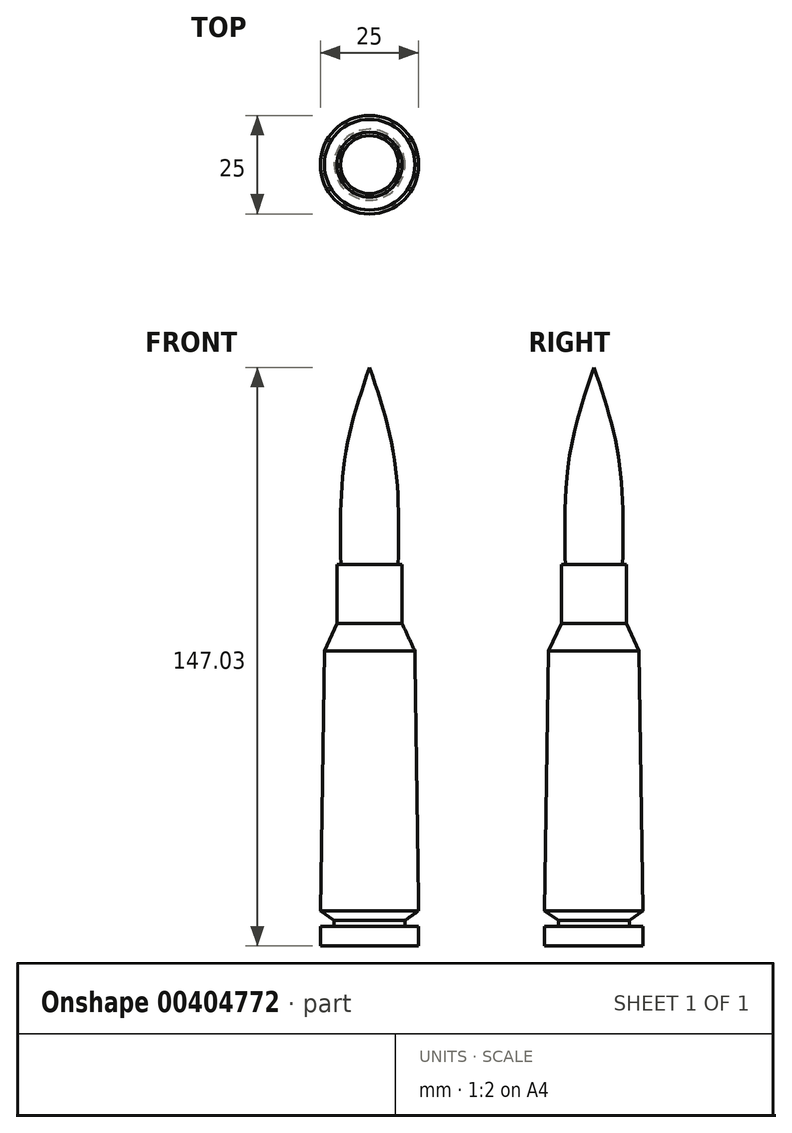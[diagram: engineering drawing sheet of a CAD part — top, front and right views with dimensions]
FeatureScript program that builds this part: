
annotation { "Feature Type Name" : "Feature", "Feature Type Description" : "" }
export const myFeature = defineFeature(function(context is Context, id is Id, definition is map)
    precondition{}
    {
        {
            var Q0;
            Q0=qCreatedBy(makeId("Top.planeOp"),FACE);
            var sketch = newSketch(context, id + "F0", { "sketchPlane" : qUnion([Q0])});
            skCircle(sketch, "E0", {"center": v(0, 0) * mm, "radius": 12.5 * mm});
            skSolve(sketch);
        }
        {
            var Q0;
            Q0=qSketchRegion(id+"F0",true);
            extrude(context, id + "F1", {"entities" : qUnion([Q0]), "depth" : 5 * mm});
        }
        {
            var Q0;
            Q0=makeQuery(id+"F1.opExtrude","CAP_FACE",FACE,{"disambiguationData":[OSD([sQuery(id+"F0.wireOp",EDGE,"E0")])],"isStart":false});
            var sketch = newSketch(context, id + "F2", { "sketchPlane" : qUnion([Q0])});
            skCircle(sketch, "E1", {"center": v(0, 0) * mm, "radius": 9 * mm});
            skSolve(sketch);
        }
        {
            var Q0;
            Q0=qSketchRegion(id+"F2",true);
            extrude(context, id + "F3", {"entities" : qUnion([Q0]), "operationType" : NewBodyOperationType.ADD, "depth" : 1.5 * mm});
        }
        {
            var Q0;
            Q0=qCreatedBy(makeId("Top.planeOp"),FACE);
            cPlane(context, id + "F4", {"entities" : qUnion([Q0]), "cplaneType" : CPlaneType.OFFSET, "offset" : 9 * mm, "width" : 150 * mm, "height" : 150 * mm});
        }
        {
            var Q0;
            Q0=qCreatedBy(id+"F4.planeOp",FACE);
            var sketch = newSketch(context, id + "F5", { "sketchPlane" : qUnion([Q0])});
            skCircle(sketch, "E2", {"center": v(0, 0) * mm, "radius": 12.5 * mm});
            skSolve(sketch);
        }
        {
            var Q1;
            Q1=makeQuery(id+"F3.opExtrude","CAP_FACE",FACE,{"disambiguationData":[OSD([sQuery(id+"F2.wireOp",EDGE,"E1")])],"isStart":false});
            var Q2;
            Q2=makeQuery(id+"F5.imprint","IMPRINT",FACE,{"disambiguationData":[TD([[makeQuery(id+"F5.imprint","IMPRINT",EDGE,{"derivedFrom":sQuery(id+"F5.wireOp",EDGE,"E2")}),1.0]])]});
            loft(context, id + "F6", {"operationType" : NewBodyOperationType.ADD, "sheetProfilesArray" : [{ "sheetProfileEntities" : qUnion([Q1]) }, { "sheetProfileEntities" : qUnion([Q2]) }]});
        }
        {
            var Q0;
            Q0=qCreatedBy(makeId("Top.planeOp"),FACE);
            cPlane(context, id + "F7", {"entities" : qUnion([Q0]), "cplaneType" : CPlaneType.OFFSET, "offset" : 75 * mm, "width" : 150 * mm, "height" : 150 * mm});
        }
        {
            var Q0;
            Q0=qCreatedBy(id+"F7.planeOp",FACE);
            var sketch = newSketch(context, id + "F8", { "sketchPlane" : qUnion([Q0])});
            skCircle(sketch, "E3", {"center": v(0, 0) * mm, "radius": 11.5 * mm});
            skSolve(sketch);
        }
        {
            var Q1;
            Q1=makeQuery(id+"F8.imprint","IMPRINT",FACE,{"disambiguationData":[TD([[makeQuery(id+"F8.imprint","IMPRINT",EDGE,{"derivedFrom":sQuery(id+"F8.wireOp",EDGE,"E3")}),1.0]])]});
            var Q2;
            Q2=makeQuery(id+"F6.opLoft","CAP_FACE",FACE,{"disambiguationData":[OSD([makeQuery(id+"F5.imprint","IMPRINT",FACE,{"disambiguationData":[TD([[makeQuery(id+"F5.imprint","IMPRINT",EDGE,{"derivedFrom":sQuery(id+"F5.wireOp",EDGE,"E2")}),1.0]])]})])],"isStart":true});
            loft(context, id + "F9", {"operationType" : NewBodyOperationType.ADD, "sheetProfilesArray" : [{ "sheetProfileEntities" : qUnion([Q1]) }, { "sheetProfileEntities" : qUnion([Q2]) }]});
        }
        {
            var Q0;
            Q0=qCreatedBy(makeId("Top.planeOp"),FACE);
            cPlane(context, id + "F10", {"entities" : qUnion([Q0]), "cplaneType" : CPlaneType.OFFSET, "offset" : 82 * mm, "width" : 150 * mm, "height" : 150 * mm});
        }
        {
            var Q0;
            Q0=qCreatedBy(id+"F10.planeOp",FACE);
            var sketch = newSketch(context, id + "F11", { "sketchPlane" : qUnion([Q0])});
            skCircle(sketch, "E4", {"center": v(0, 0) * mm, "radius": 8.25 * mm});
            skSolve(sketch);
        }
        {
            var Q1;
            Q1=makeQuery(id+"F11.imprint","IMPRINT",FACE,{"disambiguationData":[TD([[makeQuery(id+"F11.imprint","IMPRINT",EDGE,{"derivedFrom":sQuery(id+"F11.wireOp",EDGE,"E4")}),1.0]])]});
            var Q2;
            Q2=makeQuery(id+"F9.opLoft","CAP_FACE",FACE,{"disambiguationData":[OSD([makeQuery(id+"F8.imprint","IMPRINT",FACE,{"disambiguationData":[TD([[makeQuery(id+"F8.imprint","IMPRINT",EDGE,{"derivedFrom":sQuery(id+"F8.wireOp",EDGE,"E3")}),1.0]])]})])],"isStart":true});
            loft(context, id + "F12", {"operationType" : NewBodyOperationType.ADD, "sheetProfilesArray" : [{ "sheetProfileEntities" : qUnion([Q1]) }, { "sheetProfileEntities" : qUnion([Q2]) }]});
        }
        {
            var Q0;
            Q0=makeQuery(id+"F12.opLoft","CAP_FACE",FACE,{"disambiguationData":[OSD([makeQuery(id+"F11.imprint","IMPRINT",FACE,{"disambiguationData":[TD([[makeQuery(id+"F11.imprint","IMPRINT",EDGE,{"derivedFrom":sQuery(id+"F11.wireOp",EDGE,"E4")}),1.0]])]})])],"isStart":true});
            extrude(context, id + "F13", {"entities" : qUnion([Q0]), "operationType" : NewBodyOperationType.ADD, "depth" : 15 * mm});
        }
        {
            var Q0;
            Q0=qCreatedBy(makeId("Right.planeOp"),FACE);
            var sketch = newSketch(context, id + "F14", { "sketchPlane" : qUnion([Q0])});
            skFitSpline(sketch, "E5", {"points": [v(0, 147.03) * mm, v(6.26, 124.16) * mm, v(7.28, 96.96) * mm], "startDerivative": vector(15.63, -46.12) * mm, "endDerivative": vector(-0.88, -53.94) * mm});
            skFitSpline(sketch, "E6", {"points": [v(7.28, 96.96) * mm, v(0, 96.96) * mm], "startDerivative": vector(-7.28, 0) * mm, "endDerivative": vector(-7.28, 0) * mm});
            skLineSegment(sketch, "E7", {"start": v(0, 147.03) * mm, "end": v(0, 96.96) * mm});
            skSolve(sketch);
        }
        {
            var Q0;
            Q0=qSketchRegion(id+"F14",true);
            var Q1;
            Q1=makeQuery(id+"F14.imprint","IMPRINT",FACE,{"disambiguationData":[TD([[makeQuery(id+"F14.imprint","IMPRINT",EDGE,{"derivedFrom":sQuery(id+"F14.wireOp",EDGE,"E5")}),-1.0]])]});
            var Q2;
            Q2=sQuery(id+"F14.wireOp",EDGE,"E7");
            revolve(context, id + "F15", {"operationType" : NewBodyOperationType.ADD, "entities" : qUnion([Q0, Q1]), "axis" : qUnion([Q2]), "revolveType" : RevolveType.FULL});
        }
    });
